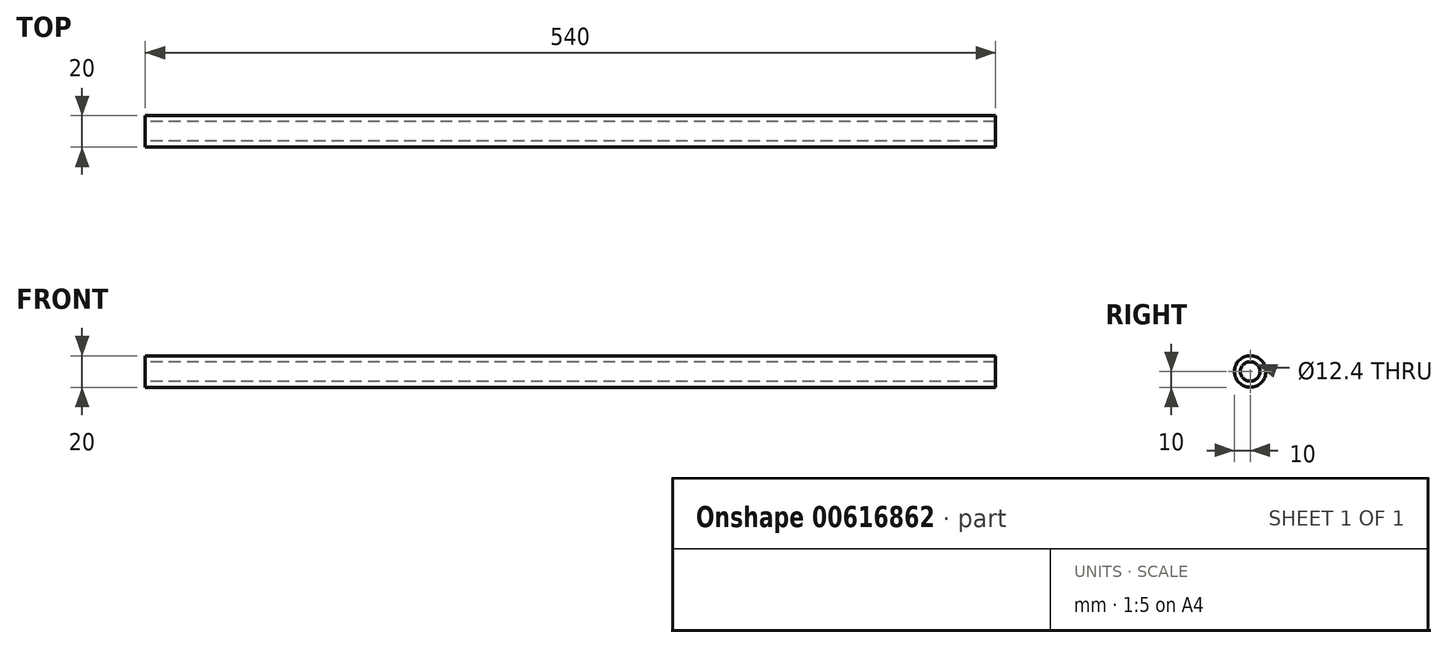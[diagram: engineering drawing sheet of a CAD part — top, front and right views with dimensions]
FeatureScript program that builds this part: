
annotation { "Feature Type Name" : "Feature", "Feature Type Description" : "" }
export const myFeature = defineFeature(function(context is Context, id is Id, definition is map)
    precondition{}
    {
        {
            var Q0;
            Q0=qCreatedBy(makeId("Right.planeOp"),FACE);
            var sketch = newSketch(context, id + "F0", { "sketchPlane" : qUnion([Q0])});
            skCircle(sketch, "E0", {"center": v(0, 0) * mm, "radius": 10 * mm});
            skCircle(sketch, "E1", {"center": v(0, 0) * mm, "radius": 6.2 * mm});
            skSolve(sketch);
        }
        {
            var Q0;
            Q0=qSketchRegion(id+"F0",true);
            extrude(context, id + "F1", {"entities" : qUnion([Q0]), "depth" : 540 * mm, "offsetDistance" : 25 * mm, "symmetric" : true});
        }
    });
